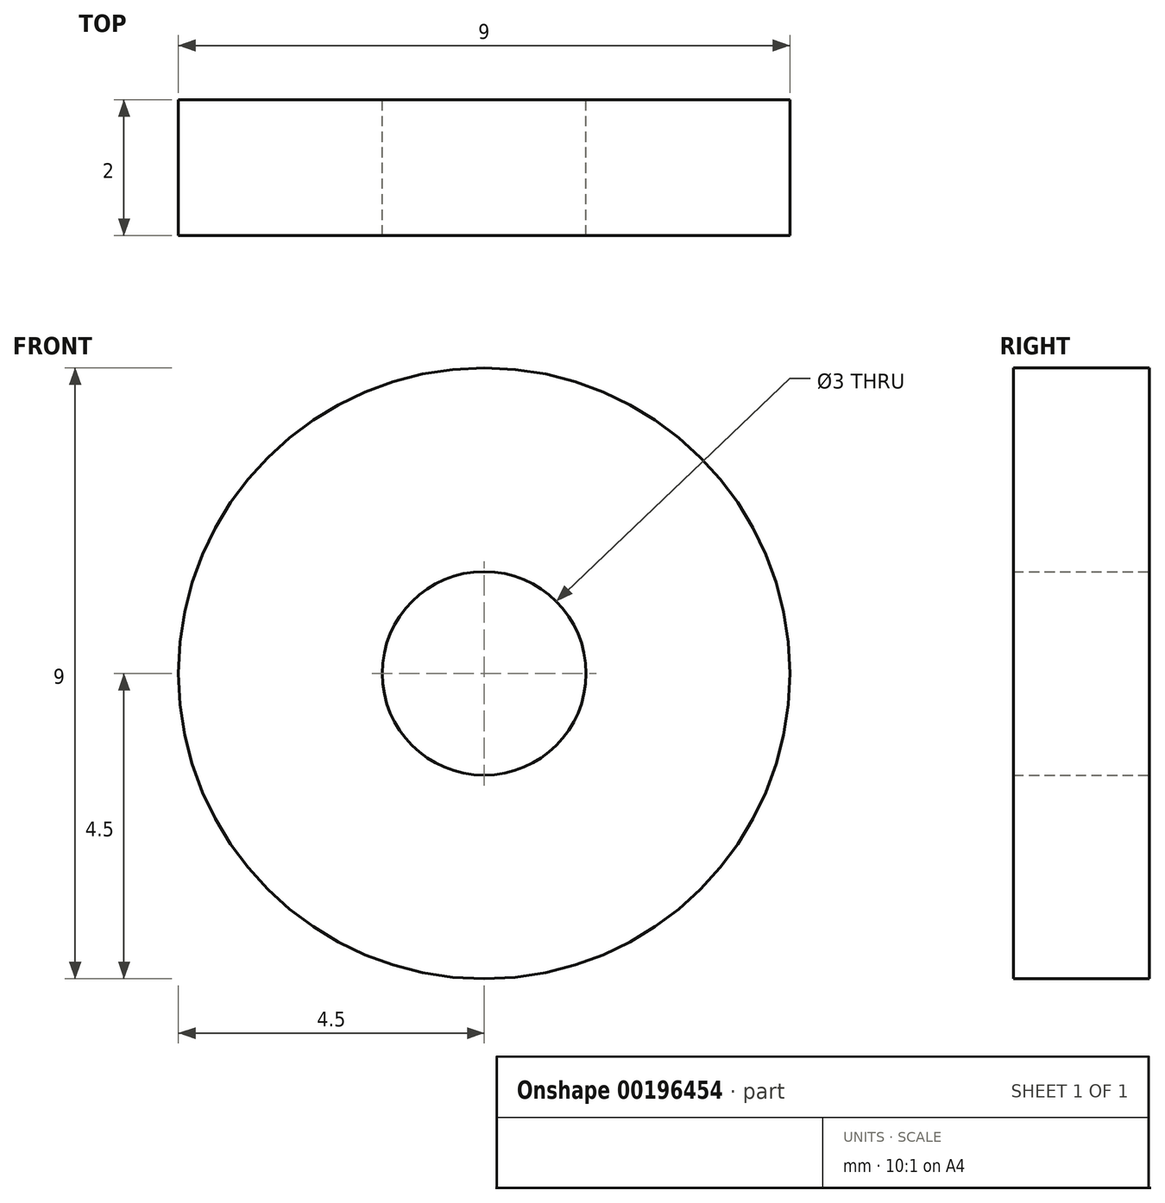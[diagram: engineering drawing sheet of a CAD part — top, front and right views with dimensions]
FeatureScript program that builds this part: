
annotation { "Feature Type Name" : "Feature", "Feature Type Description" : "" }
export const myFeature = defineFeature(function(context is Context, id is Id, definition is map)
    precondition{}
    {
        {
            var Q0;
            Q0=qCreatedBy(makeId("Front.planeOp"),FACE);
            var sketch = newSketch(context, id + "F0", { "sketchPlane" : qUnion([Q0])});
            skCircle(sketch, "E0", {"center": v(0, 0) * mm, "radius": 1.5 * mm});
            skCircle(sketch, "E1", {"center": v(0, 0) * mm, "radius": 4.5 * mm});
            skSolve(sketch);
        }
        {
            var Q0;
            Q0 = qSketchRegion(id + "F0", true);
            extrude(context, id + "F1", {"entities" : qUnion([Q0]), "depth" : 2 * mm});
        }
    });
